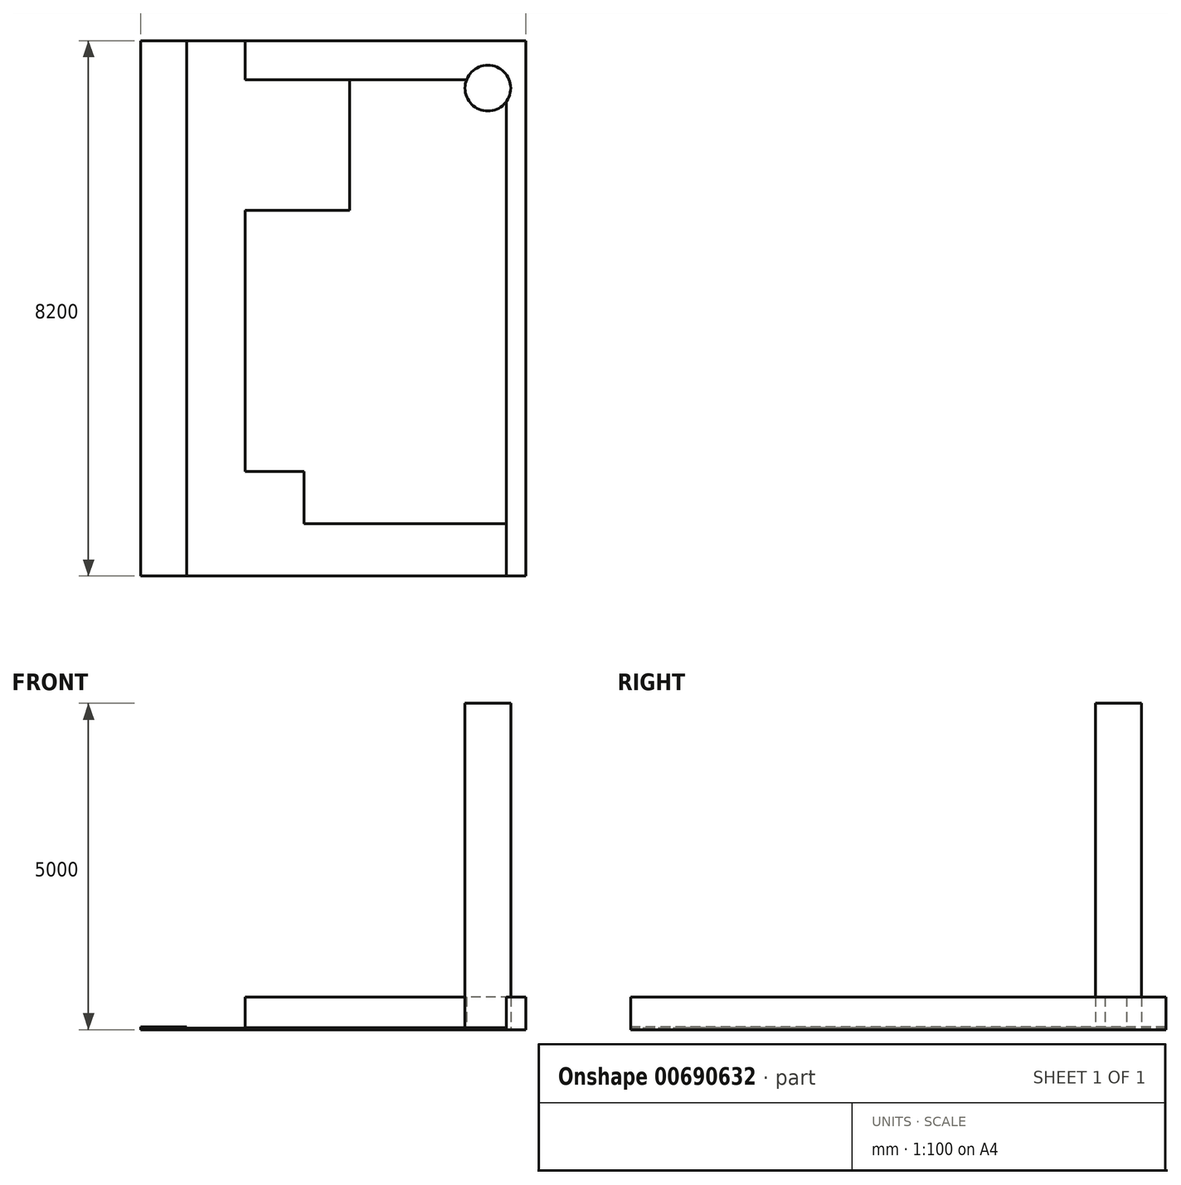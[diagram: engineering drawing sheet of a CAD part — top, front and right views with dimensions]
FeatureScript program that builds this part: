
annotation { "Feature Type Name" : "Feature", "Feature Type Description" : "" }
export const myFeature = defineFeature(function(context is Context, id is Id, definition is map)
    precondition{}
    {
        {
            var Q0;
            Q0=qCreatedBy(makeId("Top.planeOp"),FACE);
            var sketch = newSketch(context, id + "F0", { "sketchPlane" : qUnion([Q0])});
            skLineSegment(sketch, "E0.bottom", {"start": v(0, 0) * mm, "end": v(5900, 0) * mm});
            skLineSegment(sketch, "E0.top", {"start": v(0, -8200) * mm, "end": v(5900, -8200) * mm});
            skLineSegment(sketch, "E0.left", {"start": v(0, 0) * mm, "end": v(0, -8200) * mm});
            skLineSegment(sketch, "E0.right", {"start": v(5900, 0) * mm, "end": v(5900, -8200) * mm});
            skLineSegment(sketch, "E1", {"start": v(700, 0) * mm, "end": v(700, -8200) * mm});
            skLineSegment(sketch, "E2", {"start": v(1600, 0) * mm, "end": v(1600, -600) * mm});
            skLineSegment(sketch, "E3", {"start": v(1600, -6600) * mm, "end": v(2500, -6600) * mm});
            skLineSegment(sketch, "E4", {"start": v(2500, -6600) * mm, "end": v(2500, -7400) * mm});
            skLineSegment(sketch, "E5", {"start": v(2500, -7400) * mm, "end": v(5600, -7400) * mm});
            skLineSegment(sketch, "E6", {"start": v(5600, -7400) * mm, "end": v(5600, -8200) * mm});
            skLineSegment(sketch, "E7", {"start": v(5600, -7400) * mm, "end": v(5600, 0) * mm});
            skLineSegment(sketch, "E8", {"start": v(1600, -600) * mm, "end": v(3200, -600) * mm});
            skLineSegment(sketch, "E9", {"start": v(3200, -600) * mm, "end": v(3200, -2600) * mm});
            skLineSegment(sketch, "E10", {"start": v(3200, -2600) * mm, "end": v(1600, -2600) * mm});
            skLineSegment(sketch, "E11", {"start": v(3200, -600) * mm, "end": v(5600, -600) * mm});
            skCircle(sketch, "E12", {"center": v(5315.24, -726.04) * mm, "radius": 350 * mm});
            skLineSegment(sketch, "E13", {"start": v(4500, -600) * mm, "end": v(4500, -1600) * mm, "construction": true});
            skLineSegment(sketch, "E14", {"start": v(4500, -1600) * mm, "end": v(5600, -1600) * mm, "construction": true});
            skLineSegment(sketch, "E15.trimOffspring", {"start": v(1600, -2600) * mm, "end": v(1600, -6600) * mm});
            skSolve(sketch);
        }
        {
            var Q0;
            {var subQ6=sQuery(id+"F0.wireOp",EDGE,"E2");Q0=makeQuery(id+"F0.imprint","IMPRINT",FACE,{"disambiguationData":[TD([[makeQuery(id+"F0.imprint","IMPRINT",EDGE,{"derivedFrom":subQ6}),1.0]])]});}
            var Q1;
            {var subQ1=sQuery(id+"F0.wireOp",EDGE,"E0.right");Q1=makeQuery(id+"F0.imprint","IMPRINT",FACE,{"disambiguationData":[TD([[makeQuery(id+"F0.imprint","IMPRINT",EDGE,{"derivedFrom":subQ1}),-1.0]])]});}
            extrude(context, id + "F1", {"entities" : qUnion([Q0, Q1]), "depth" : 500 * mm, "offsetDistance" : 25 * mm});
        }
        {
            var Q0;
            {var subQ1=sQuery(id+"F0.wireOp",EDGE,"E1");Q0=makeQuery(id+"F0.imprint","IMPRINT",FACE,{"disambiguationData":[TD([[makeQuery(id+"F0.imprint","IMPRINT",EDGE,{"derivedFrom":subQ1}),1.0]])]});}
            extrude(context, id + "F2", {"entities" : qUnion([Q0]), "depth" : 25 * mm, "offsetDistance" : 25 * mm});
        }
        {
            var Q0;
            {var subQ0=sQuery(id+"F0.wireOp",EDGE,"E0.left");Q0=makeQuery(id+"F0.imprint","IMPRINT",FACE,{"disambiguationData":[TD([[makeQuery(id+"F0.imprint","IMPRINT",EDGE,{"derivedFrom":subQ0}),1.0]])]});}
            extrude(context, id + "F3", {"entities" : qUnion([Q0]), "depth" : 45 * mm, "offsetDistance" : 25 * mm});
        }
        {
            var Q0;
            Q0=makeQuery(id+"F0.imprint","IMPRINT",FACE,{"disambiguationData":[TD([[makeQuery(id+"F0.imprint","IMPRINT",EDGE,{"derivedFrom":sQuery(id+"F0.wireOp",EDGE,"E3")}),1.0]])]});
            extrude(context, id + "F4", {"entities" : qUnion([Q0]), "depth" : 30 * mm, "offsetDistance" : 25 * mm});
        }
        {
            var Q0;
            {var subQ0=sQuery(id+"F0.wireOp",EDGE,"E11");var subQ1=sQuery(id+"F0.wireOp",EDGE,"E7");var subQ2=makeQuery(id+"F0.imprint","INTERSECT",VERTEX,{"derivedFrom":[subQ1,subQ0]});Q0=makeQuery(id+"F0.imprint","IMPRINT",FACE,{"disambiguationData":[TD([[makeQuery(id+"F0.imprint","IMPRINT",EDGE,{"disambiguationData":[TD([[subQ2,-1.0]])],"derivedFrom":subQ1}),1.0]])]});}
            var Q1;
            {var subQ0=sQuery(id+"F0.wireOp",EDGE,"E7");var subQ1=makeQuery(id+"F0.imprint","INTERSECT",VERTEX,{"derivedFrom":[subQ0,sQuery(id+"F0.wireOp",EDGE,"E11")]});Q1=makeQuery(id+"F0.imprint","IMPRINT",FACE,{"disambiguationData":[TD([[makeQuery(id+"F0.imprint","IMPRINT",EDGE,{"disambiguationData":[TD([[subQ1,1.0]])],"derivedFrom":subQ0}),-1.0]])]});}
            var Q2;
            {var subQ0=sQuery(id+"F0.wireOp",EDGE,"E11");var subQ1=sQuery(id+"F0.wireOp",EDGE,"E7");var subQ2=makeQuery(id+"F0.imprint","INTERSECT",VERTEX,{"derivedFrom":[subQ1,subQ0]});Q2=makeQuery(id+"F0.imprint","IMPRINT",FACE,{"disambiguationData":[TD([[makeQuery(id+"F0.imprint","IMPRINT",EDGE,{"disambiguationData":[TD([[subQ2,1.0]])],"derivedFrom":subQ1}),1.0]])]});}
            extrude(context, id + "F5", {"entities" : qUnion([Q0, Q1, Q2]), "depth" : 5000 * mm, "offsetDistance" : 25 * mm});
        }
    });
